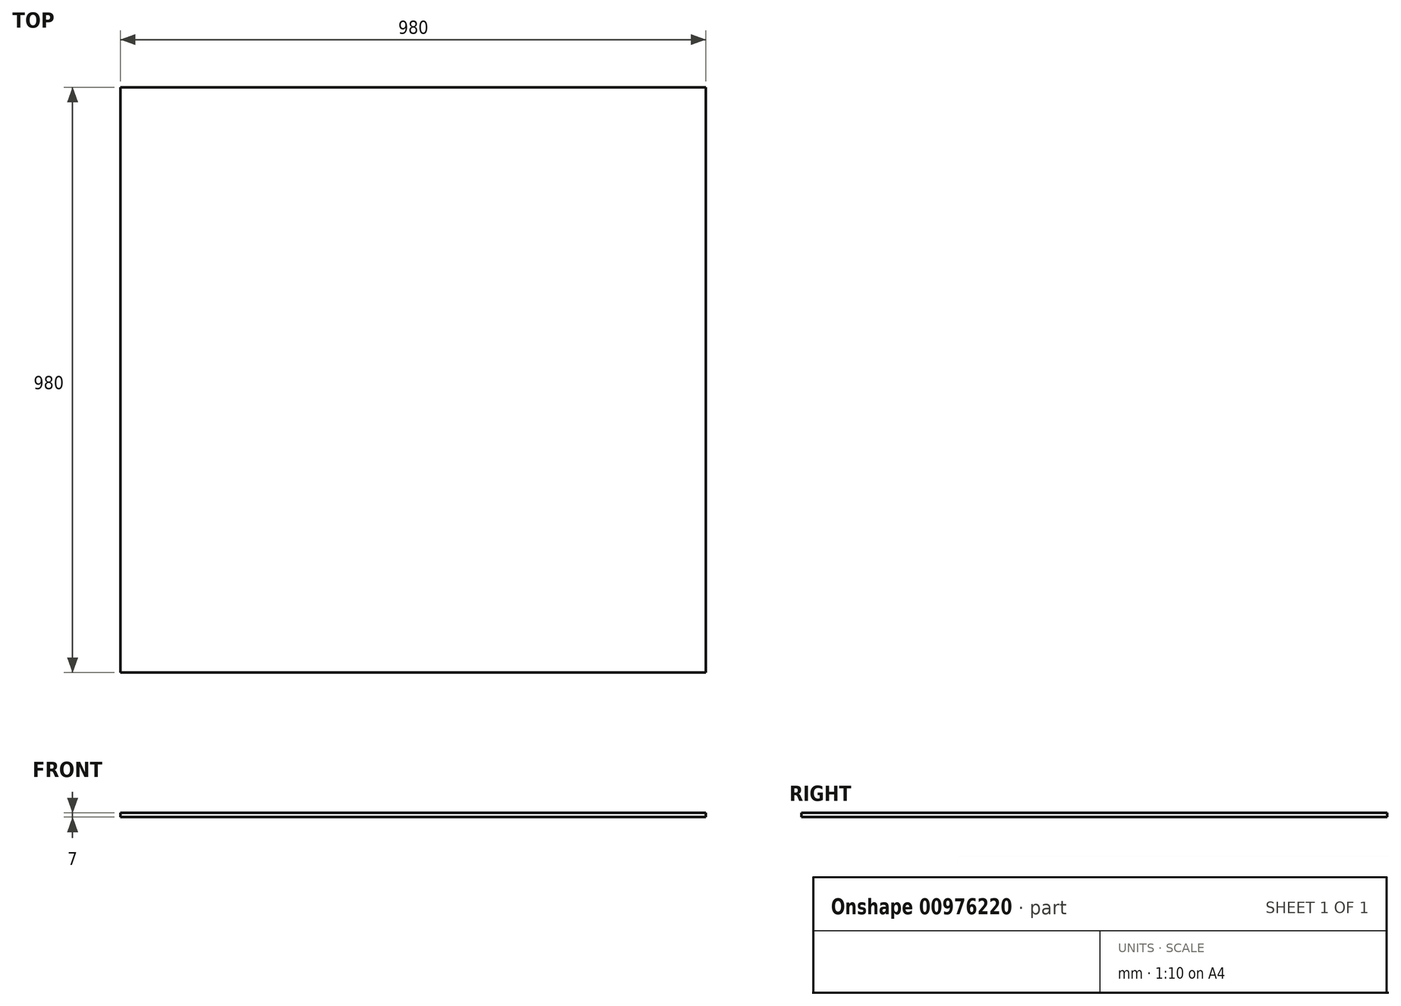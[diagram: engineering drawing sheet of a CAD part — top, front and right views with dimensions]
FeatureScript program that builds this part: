
annotation { "Feature Type Name" : "Feature", "Feature Type Description" : "" }
export const myFeature = defineFeature(function(context is Context, id is Id, definition is map)
    precondition{}
    {
        {
            var Q0;
            Q0=qCreatedBy(makeId("Top.planeOp"),FACE);
            var sketch = newSketch(context, id + "F0", { "sketchPlane" : qUnion([Q0])});
            skLineSegment(sketch, "E0.bottom", {"start": v(490, 490) * mm, "end": v(-490, 490) * mm});
            skLineSegment(sketch, "E0.top", {"start": v(490, -490) * mm, "end": v(-490, -490) * mm});
            skLineSegment(sketch, "E0.left", {"start": v(490, 490) * mm, "end": v(490, -490) * mm});
            skLineSegment(sketch, "E0.right", {"start": v(-490, 490) * mm, "end": v(-490, -490) * mm});
            skPoint(sketch, "E0.middle", {"position": v(0, 0) * mm});
            skSolve(sketch);
        }
        {
            var Q0;
            Q0=makeQuery(id+"F0.imprint","IMPRINT",FACE,{"disambiguationData":[TD([[makeQuery(id+"F0.imprint","IMPRINT",EDGE,{"derivedFrom":sQuery(id+"F0.wireOp",EDGE,"E0.bottom")}),1.0]])]});
            extrude(context, id + "F1", {"entities" : qUnion([Q0]), "depth" : 7 * mm, "offsetDistance" : 25 * mm});
        }
    });
